# Revit family: 61807-F-L
name_source: partatom
category: Meble
units: mm (PartAtom-declared; Revit-internal decimal feet)

## family parameters
Numer OmniClass = 23.40.20.00
Oparty na płaszczyźnie roboczej = Nie
Punkt obliczania pomieszczeń = Nie
Tnij formami wycięć po wczytaniu = Nie
Tytuł OmniClass = General Furniture and Specialties
Współdzielony = Nie
Zawsze pionowo = Tak

## types (1)
- 61807-f-l
    Domyślna rzędna = 0 cm
    Height = 55 cm
    Hosted on larslaj.com = https://larslaj.com
    Kobenhagen Materials = larslaj.com/bim
    Lenght = 181 cm
    Maintenance = We recommend to examine and tighten all screws and bolt clamps after a few weeks’ use. In order to prevent cracks and to extend the life of the wood, it is recommended that the wood details should be oiled every 3-5 years.
    Material = Larch, stainless steel, powder coated steel
    Model = 61807-F-L
    Opis = Holmen Bench w/ Plant Case
    Producent = Lars Laj
    Product Groups = Benches
    Product line = Holmen
    Seat height = 45 cm
    Size = 105 L
    URL = https://kobenhagen.com
    Weight = 35 kg
    Width = 83 cm
    metal = Kobenhagen RAL 9010
    wood = Kobenhagen Wood - Larch
